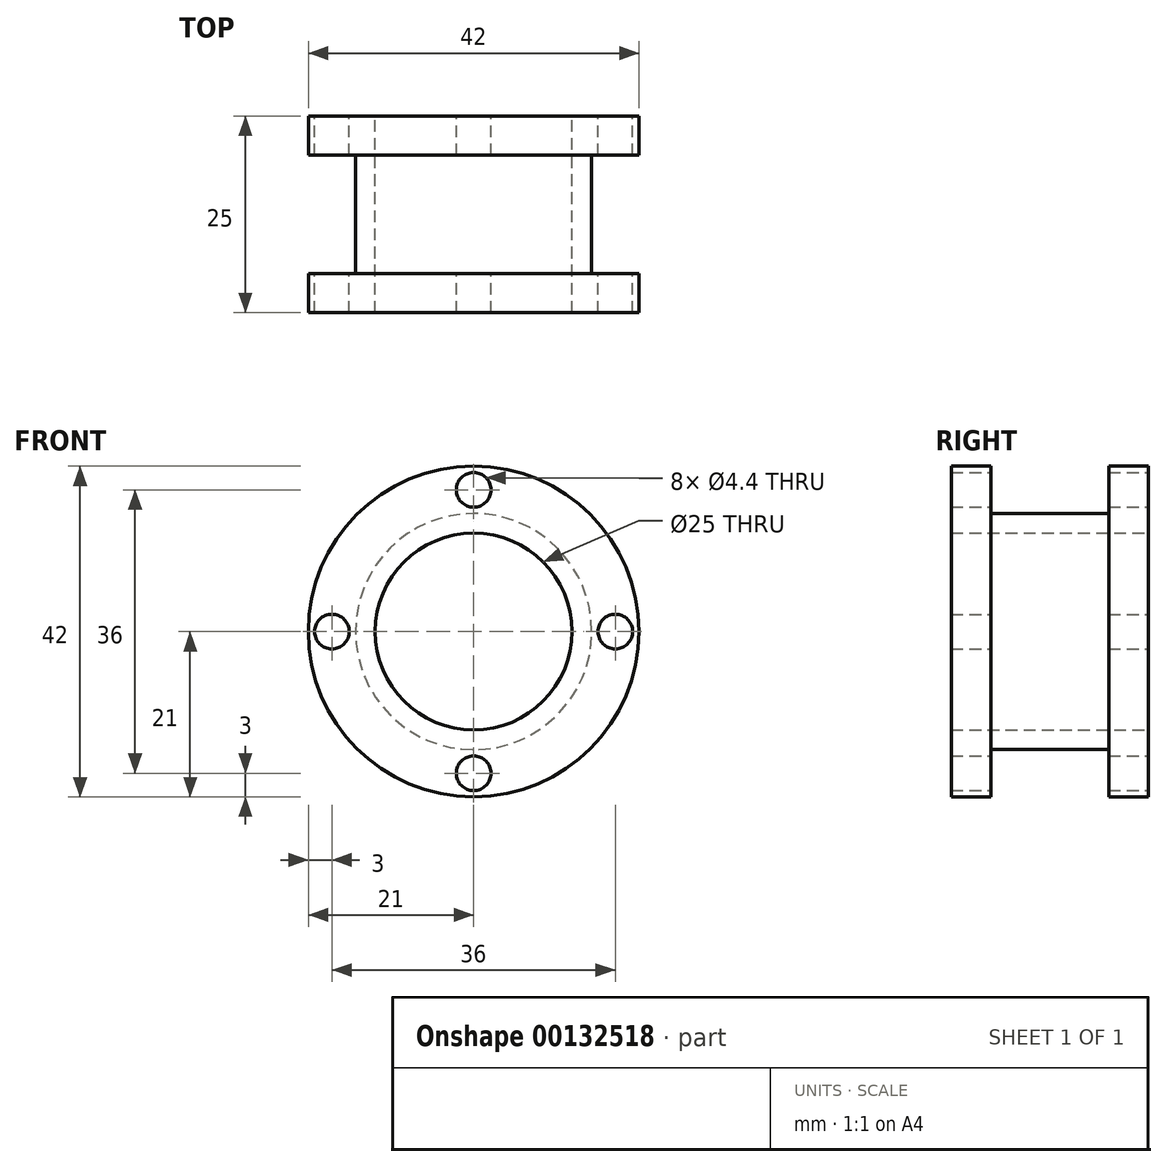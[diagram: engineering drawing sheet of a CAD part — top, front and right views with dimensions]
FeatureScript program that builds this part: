
annotation { "Feature Type Name" : "Feature", "Feature Type Description" : "" }
export const myFeature = defineFeature(function(context is Context, id is Id, definition is map)
    precondition{}
    {
        {
            var Q0;
            Q0=qCreatedBy(makeId("Front.planeOp"),FACE);
            var sketch = newSketch(context, id + "F0", { "sketchPlane" : qUnion([Q0])});
            skCircle(sketch, "E0", {"center": v(0, 0) * mm, "radius": 15 * mm});
            skCircle(sketch, "E1", {"center": v(0, 0) * mm, "radius": 12.5 * mm});
            skCircle(sketch, "E2", {"center": v(0, 0) * mm, "radius": 21 * mm});
            skPoint(sketch, "E3", {"position": v(0, -18) * mm});
            skPoint(sketch, "E4", {"position": v(18, 0) * mm});
            skPoint(sketch, "E5", {"position": v(0, 18) * mm});
            skPoint(sketch, "E6", {"position": v(-18, 0) * mm});
            skSolve(sketch);
        }
        {
            var Q0;
            Q0=makeQuery(id+"F0.imprint","IMPRINT",FACE,{"disambiguationData":[TD([[makeQuery(id+"F0.imprint","IMPRINT",EDGE,{"derivedFrom":sQuery(id+"F0.wireOp",EDGE,"E0")}),1.0]])]});
            extrude(context, id + "F1", {"entities" : qUnion([Q0]), "depth" : 25 * mm});
        }
        {
            var Q0;
            Q0=sQuery(id+"F0.wireOp",EDGE,"E1");
            extrude(context, id + "F2", {"bodyType" : ToolBodyType.SURFACE, "surfaceEntities" : qUnion([Q0]), "depth" : 25 * mm});
        }
        {
            var Q0;
            Q0=makeQuery(id+"F0.imprint","IMPRINT",FACE,{"disambiguationData":[TD([[makeQuery(id+"F0.imprint","IMPRINT",EDGE,{"derivedFrom":sQuery(id+"F0.wireOp",EDGE,"E0")}),-1.0]])]});
            extrude(context, id + "F3", {"entities" : qUnion([Q0]), "operationType" : NewBodyOperationType.ADD, "depth" : 5 * mm});
        }
        {
            var Q0;
            Q0=makeQuery(id+"F1.opExtrude","CAP_FACE",FACE,{"disambiguationData":[OSD([sQuery(id+"F0.wireOp",EDGE,"E0"),sQuery(id+"F0.wireOp",EDGE,"E1")])],"isStart":false});
            var sketch = newSketch(context, id + "F4", { "sketchPlane" : qUnion([Q0])});
            skCircle(sketch, "E7", {"center": v(0, 0) * mm, "radius": 21 * mm});
            skSolve(sketch);
        }
        {
            var Q0;
            Q0=makeQuery(id+"F4.imprint","IMPRINT",FACE,{"disambiguationData":[TD([[makeQuery(id+"F4.imprint","IMPRINT",EDGE,{"derivedFrom":sQuery(id+"F4.wireOp",EDGE,"E7")}),1.0]])]});
            extrude(context, id + "F5", {"entities" : qUnion([Q0]), "operationType" : NewBodyOperationType.ADD, "oppositeDirection" : true, "depth" : 5 * mm});
        }
        {
            var Q0;
            Q0=sQuery(id+"F0.wireOp",VERTEX,"E6");
            var Q1;
            Q1=sQuery(id+"F0.wireOp",VERTEX,"E3");
            var Q2;
            Q2=sQuery(id+"F0.wireOp",VERTEX,"E4");
            var Q3;
            Q3=sQuery(id+"F0.wireOp",VERTEX,"E5");
            var Q4;
            Q4=makeQuery(id+"F1.opExtrude","SWEPT_BODY",BODY,{"disambiguationData":[OSD([sQuery(id+"F0.wireOp",EDGE,"E0"),sQuery(id+"F0.wireOp",EDGE,"E1")])]});
            hole(context, id + "F6", {"style" : HoleStyle.SIMPLE, "endStyle" : HoleEndStyle.THROUGH, "oppositeDirection" : true, "holeDiameter" : 4.4 * mm, "locations" : qUnion([Q0, Q1, Q2, Q3]), "scope" : qUnion([Q4]), "isTappedThrough" : true});
        }
    });
